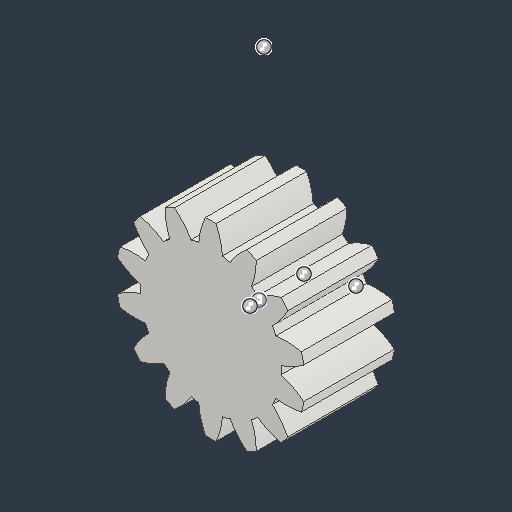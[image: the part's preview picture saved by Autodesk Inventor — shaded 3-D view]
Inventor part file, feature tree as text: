
AUTODESK INVENTOR PART (.ipt)
format: ipt  version: 2024.3 (Build 283343000, 343)  size: 188,928 bytes
history: native  units: mm (DEFAULTED — no unit token found)
features: plane x3, other x3, extrude x1, sketch x1
ambient origin geometry x8: Origin, YZ Plane, XZ Plane, XY Plane, X Axis, Y Axis, Z Axis, Center Point
bodies: Solid1 (feature_tree)
feature tree (8):
  extrude  "Extrusion1"  Depth=16.0mm TaperAngle=0.0deg
  plane  "Work Plane2"
  plane  "Work Plane8"
  plane  "Work Plane9"
  other  "Spur Gear"
  sketch  "Sketch1"  dims[d0=33.307842mm d1=16.0mm d2=0.0mm d3=28.0mm d4=10.0mm d5=0.0mm d16=29.6mm d17=0.0mm d34=2.243995mm d39=0.0mm d41=0.0mm d43=29.6mm d46=29.6mm d47=0.0mm d48=0.0mm]
  other  "Srf1"
  other  "Pitch Diameter"
